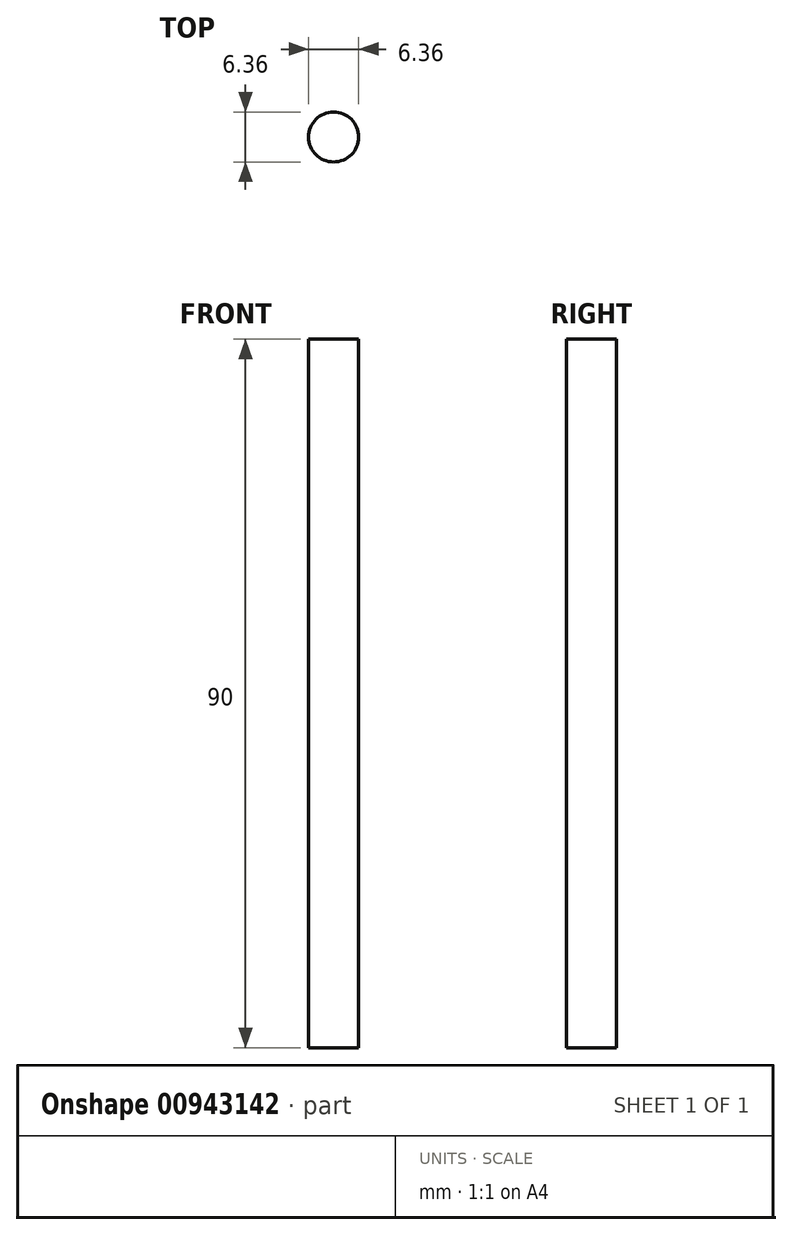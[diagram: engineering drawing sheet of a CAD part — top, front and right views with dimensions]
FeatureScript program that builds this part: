
annotation { "Feature Type Name" : "Feature", "Feature Type Description" : "" }
export const myFeature = defineFeature(function(context is Context, id is Id, definition is map)
    precondition{}
    {
        {
            var Q0;
            Q0=qCreatedBy(makeId("Top.planeOp"),FACE);
            var sketch = newSketch(context, id + "F0", { "sketchPlane" : qUnion([Q0])});
            skCircle(sketch, "E0", {"center": v(0, 0) * mm, "radius": 3.17 * mm});
            skSolve(sketch);
        }
        {
            var Q0;
            Q0 = qSketchRegion(id + "F0", true);
            extrude(context, id + "F1", {"entities" : qUnion([Q0]), "depth" : 90 * mm, "offsetDistance" : 25 * mm});
        }
    });
